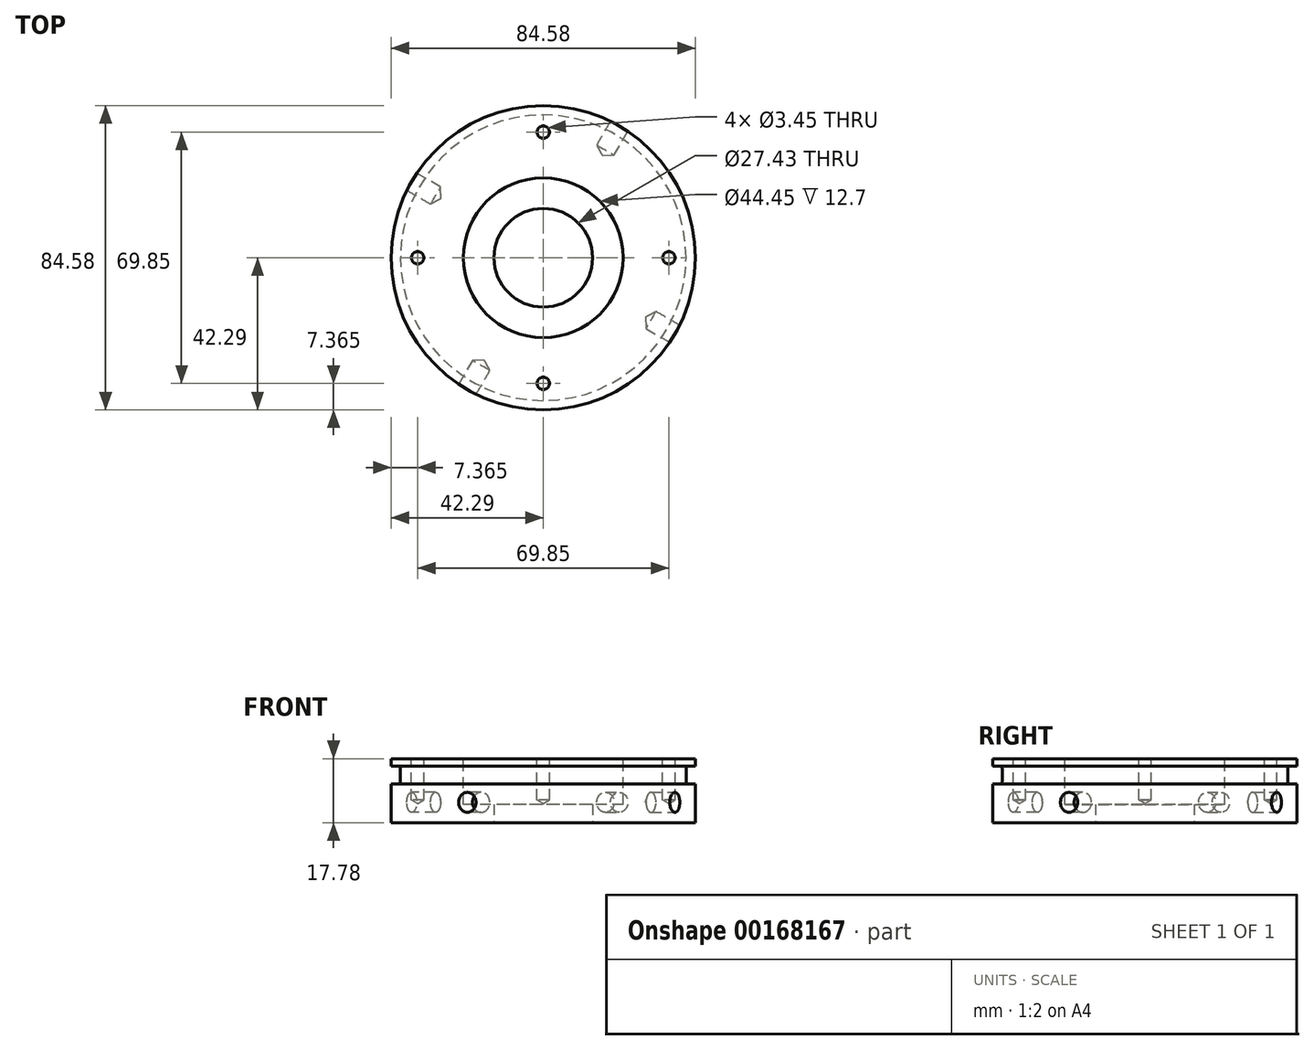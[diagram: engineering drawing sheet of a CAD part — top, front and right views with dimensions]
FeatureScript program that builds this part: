
annotation { "Feature Type Name" : "Feature", "Feature Type Description" : "" }
export const myFeature = defineFeature(function(context is Context, id is Id, definition is map)
    precondition{}
    {
        {
            var Q0;
            Q0=qCreatedBy(makeId("Top.planeOp"),FACE);
            var sketch = newSketch(context, id + "F0", { "sketchPlane" : qUnion([Q0])});
            skCircle(sketch, "E0", {"center": v(0, 0) * mm, "radius": 42.3 * mm});
            skSolve(sketch);
        }
        {
            var Q0;
            Q0=makeQuery(id+"F0.imprint","IMPRINT",FACE,{"disambiguationData":[TD([[makeQuery(id+"F0.imprint","IMPRINT",EDGE,{"derivedFrom":sQuery(id+"F0.wireOp",EDGE,"E0")}),1.0]])]});
            extrude(context, id + "F1", {"entities" : qUnion([Q0]), "depth" : 17.78 * mm});
        }
        {
            var Q0;
            {var subQ0=makeQuery(id+"FhJubWmbG7UBd7M_1.boolean.opBoolean","COPY",FACE,{"derivedFrom":makeQuery(id+"FhJubWmbG7UBd7M_1.opExtrude","SWEPT_FACE",FACE,{"disambiguationData":[OSD([sQuery(id+"FRuIeaWD6VeLny9_1.wireOp",EDGE,"idePJaX5-tPPE-BKw2-N1m4-zZUQrY6AHjir")])]})});Q0=makeQuery(id+"FOQC5dfjhO448EJ_1.boolean.opBoolean","SPLIT",FACE,{"disambiguationData":[TD([subQ0])],"derivedFrom":makeQuery(id+"FkcieFRIapZdHPD_1.boolean.opBoolean","SPLIT",FACE,{"disambiguationData":[TD([subQ0])],"derivedFrom":makeQuery(id+"F1.opExtrude","CAP_FACE",FACE,{"disambiguationData":[OSD([sQuery(id+"F0.wireOp",EDGE,"E0")])],"isStart":false})})});}
            var sketch = newSketch(context, id + "F2", { "sketchPlane" : qUnion([Q0])});
            skCircle(sketch, "E1", {"center": v(0, 0) * mm, "radius": 34.93 * mm, "construction": true});
            skLineSegment(sketch, "E2", {"start": v(0, 0) * mm, "end": v(34.93, 0) * mm, "construction": true});
            skPoint(sketch, "E3", {"position": v(34.93, 0) * mm});
            skPoint(sketch, "E4.1.0", {"position": v(0, 34.93) * mm});
            skPoint(sketch, "E4.2.0", {"position": v(-34.93, 0) * mm});
            skPoint(sketch, "E4.3.0", {"position": v(0, -34.93) * mm});
            skSolve(sketch);
        }
        {
            var Q0;
            Q0=sQuery(id+"F2.wireOp",VERTEX,"E3");
            var Q1;
            Q1=sQuery(id+"F2.wireOp",VERTEX,"E4.3.0");
            var Q2;
            Q2=sQuery(id+"F2.wireOp",VERTEX,"E4.2.0");
            var Q3;
            Q3=sQuery(id+"F2.wireOp",VERTEX,"E4.1.0");
            var Q4;
            Q4=makeQuery(id+"F1.opExtrude","SWEPT_BODY",BODY,{"disambiguationData":[OSD([sQuery(id+"F0.wireOp",EDGE,"E0")])]});
            hole(context, id + "F3", {"style" : HoleStyle.SIMPLE, "endStyle" : HoleEndStyle.BLIND, "standardTappedOrClearance" : lookupTablePath({ "standard" : "ANSI", "engagement" : "75%", "pitch" : "32 tpi", "size" : "#8", "type" : "Tapped" }), "standardBlindInLast" : lookupTablePath({ "standard" : "ANSI", "engagement" : "75%", "pitch" : "32 tpi", "size" : "#8", "type" : "Tapped" }), "holeDiameter" : 3.45 * mm, "holeDepth" : 11.43 * mm, "locations" : qUnion([Q0, Q1, Q2, Q3]), "scope" : qUnion([Q4]), "majorDiameter" : 4.17 * mm});
        }
        {
            var Q0;
            Q0=makeQuery(id+"FOQC5dfjhO448EJ_1.boolean.opBoolean","SPLIT",FACE,{"disambiguationData":[TD([makeQuery(id+"FhJubWmbG7UBd7M_1.boolean.opBoolean","COPY",FACE,{"derivedFrom":makeQuery(id+"FhJubWmbG7UBd7M_1.opExtrude","SWEPT_FACE",FACE,{"disambiguationData":[OSD([sQuery(id+"FRuIeaWD6VeLny9_1.wireOp",EDGE,"idePJaX5-tPPE-BKw2-N1m4-zZUQrY6AHjir")])]})})])],"derivedFrom":makeQuery(id+"F1.opExtrude","CAP_FACE",FACE,{"disambiguationData":[OSD([sQuery(id+"F0.wireOp",EDGE,"E0")])],"isStart":false})});
            cPlane(context, id + "F4", {"entities" : qUnion([Q0]), "cplaneType" : CPlaneType.OFFSET, "offset" : 2.03 * mm, "oppositeDirection" : true, "width" : 152.4 * mm, "height" : 152.4 * mm});
        }
        {
            var Q0;
            Q0=qCreatedBy(id+"F4.planeOp",FACE);
            var sketch = newSketch(context, id + "F5", { "sketchPlane" : qUnion([Q0])});
            skCircle(sketch, "E5", {"center": v(0, 0) * mm, "radius": 39.7 * mm});
            skCircle(sketch, "E6.0", {"center": v(0, 0) * mm, "radius": 42.3 * mm});
            skSolve(sketch);
        }
        {
            var Q0;
            Q0=qSketchRegion(id+"F5",true);
            extrude(context, id + "F6", {"entities" : qUnion([Q0]), "operationType" : NewBodyOperationType.REMOVE, "oppositeDirection" : true, "depth" : 5 * mm});
        }
        {
            var Q0;
            Q0=makeQuery(id+"F6.boolean.opBoolean","COPY",EDGE,{"derivedFrom":makeQuery(id+"F6.opExtrude","CAP_EDGE",EDGE,{"disambiguationData":[OSD([sQuery(id+"F5.wireOp",EDGE,"E5")])],"isStart":false})});
            var Q1;
            Q1=makeQuery(id+"F6.boolean.opBoolean","COPY",EDGE,{"derivedFrom":makeQuery(id+"F6.opExtrude","CAP_EDGE",EDGE,{"disambiguationData":[OSD([sQuery(id+"F5.wireOp",EDGE,"E5")])],"isStart":true})});
            fillet(context, id + "F7", {"entities" : qUnion([Q0, Q1]), "radius" : 0.76 * mm, "tangentPropagation" : true, "allowEdgeOverflow" : false});
        }
        {
            var Q0;
            {var subQ1=sQuery(id+"F0.wireOp",EDGE,"E0");var subQ2=makeQuery(id+"F1.opExtrude","SWEPT_FACE",FACE,{"disambiguationData":[OSD([subQ1])]});Q0=makeQuery(id+"FkcieFRIapZdHPD_1.boolean.opBoolean","SPLIT",FACE,{"disambiguationData":[TD([subQ2])],"derivedFrom":makeQuery(id+"F1.opExtrude","CAP_FACE",FACE,{"disambiguationData":[OSD([subQ1])],"isStart":false})});}
            var sketch = newSketch(context, id + "F8", { "sketchPlane" : qUnion([Q0])});
            skCircle(sketch, "E7.0", {"center": v(0, 0) * mm, "radius": 42.3 * mm, "construction": true});
            skPoint(sketch, "E8", {"position": v(-21.15, -36.63) * mm});
            skLineSegment(sketch, "E9", {"start": v(0, -42.3) * mm, "end": v(0, 0) * mm, "construction": true});
            skLineSegment(sketch, "E10", {"start": v(0, 0) * mm, "end": v(-17.96, -31.1) * mm, "construction": true});
            skLineSegment(sketch, "E11", {"start": v(-17.96, -31.1) * mm, "end": v(-21.15, -36.63) * mm, "construction": true});
            skLineSegment(sketch, "E12", {"start": v(0, 0) * mm, "end": v(21.15, 36.63) * mm, "construction": true});
            skLineSegment(sketch, "E13", {"start": v(21.15, 36.63) * mm, "end": v(0, 0) * mm, "construction": true});
            skLineSegment(sketch, "E14", {"start": v(36.63, -21.15) * mm, "end": v(0, 0) * mm, "construction": true});
            skLineSegment(sketch, "E15", {"start": v(0, 0) * mm, "end": v(-36.63, 21.15) * mm, "construction": true});
            skPoint(sketch, "E16", {"position": v(21.15, 36.63) * mm});
            skPoint(sketch, "E17", {"position": v(36.63, -21.15) * mm});
            skPoint(sketch, "E18", {"position": v(-36.63, 21.15) * mm});
            skSolve(sketch);
        }
        {
            var Q0;
            Q0=qCreatedBy(makeId("Front.planeOp"),FACE);
            var sketch = newSketch(context, id + "F9", { "sketchPlane" : qUnion([Q0])});
            skLineSegment(sketch, "E19", {"start": v(0, 0) * mm, "end": v(0, 38.57) * mm, "construction": true});
            skSolve(sketch);
        }
        {
            var Q0;
            Q0=sQuery(id+"F9.wireOp",EDGE,"E19");
            cPlane(context, id + "F10", {"entities" : qUnion([Q0]), "cplaneType" : CPlaneType.LINE_ANGLE, "offset" : 25.4 * mm, "angle" : 60 * degree, "width" : 152.4 * mm, "height" : 152.4 * mm});
        }
        {
            var Q0;
            Q0=sQuery(id+"F8.wireOp",VERTEX,"E8");
            var Q1;
            Q1=qCreatedBy(id+"F10.planeOp",FACE);
            cPlane(context, id + "F11", {"entities" : qUnion([Q0, Q1]), "cplaneType" : CPlaneType.PLANE_POINT, "offset" : 25.4 * mm, "width" : 152.4 * mm, "height" : 152.4 * mm});
        }
        {
            var Q0;
            Q0=qCreatedBy(id+"F11.planeOp",FACE);
            var Q1;
            Q1=sQuery(id+"F8.wireOp",VERTEX,"E16");
            cPlane(context, id + "F12", {"entities" : qUnion([Q0, Q1]), "cplaneType" : CPlaneType.PLANE_POINT, "offset" : 25.4 * mm, "width" : 152.4 * mm, "height" : 152.4 * mm});
        }
        {
            var Q0;
            Q0=sQuery(id+"F9.wireOp",EDGE,"E19");
            cPlane(context, id + "F13", {"entities" : qUnion([Q0]), "cplaneType" : CPlaneType.LINE_ANGLE, "offset" : 25.4 * mm, "angle" : 150 * degree, "width" : 152.4 * mm, "height" : 152.4 * mm});
        }
        {
            var Q0;
            Q0=sQuery(id+"F8.wireOp",VERTEX,"E18");
            var Q1;
            Q1=qCreatedBy(id+"F13.planeOp",FACE);
            cPlane(context, id + "F14", {"entities" : qUnion([Q0, Q1]), "cplaneType" : CPlaneType.PLANE_POINT, "offset" : 25.4 * mm, "width" : 152.4 * mm, "height" : 152.4 * mm});
        }
        {
            var Q0;
            Q0=qCreatedBy(id+"F13.planeOp",FACE);
            var Q1;
            Q1=sQuery(id+"F8.wireOp",VERTEX,"E17");
            cPlane(context, id + "F15", {"entities" : qUnion([Q0, Q1]), "cplaneType" : CPlaneType.PLANE_POINT, "offset" : 25.4 * mm, "width" : 152.4 * mm, "height" : 152.4 * mm});
        }
        {
            var Q0;
            Q0=qCreatedBy(id+"F11.planeOp",FACE);
            var sketch = newSketch(context, id + "F16", { "sketchPlane" : qUnion([Q0])});
            skLineSegment(sketch, "E20", {"start": v(0, 0) * mm, "end": v(0, 5.66) * mm, "construction": true});
            skPoint(sketch, "E21", {"position": v(0, 5.66) * mm});
            skSolve(sketch);
        }
        {
            var Q0;
            Q0=qCreatedBy(id+"F12.planeOp",FACE);
            var sketch = newSketch(context, id + "F17", { "sketchPlane" : qUnion([Q0])});
            skPoint(sketch, "E22", {"position": v(0, 5.66) * mm});
            skLineSegment(sketch, "E23.0", {"start": v(0, 0) * mm, "end": v(0, 5.66) * mm, "construction": true});
            skSolve(sketch);
        }
        {
            var Q0;
            Q0=qCreatedBy(id+"F14.planeOp",FACE);
            var sketch = newSketch(context, id + "F18", { "sketchPlane" : qUnion([Q0])});
            skLineSegment(sketch, "E24", {"start": v(0, 0) * mm, "end": v(0, 5.66) * mm, "construction": true});
            skLineSegment(sketch, "E25.0", {"start": v(-42.3, 0) * mm, "end": v(-42.3, 5.66) * mm, "construction": true});
            skPoint(sketch, "E26", {"position": v(0, 5.66) * mm});
            skLineSegment(sketch, "E27", {"start": v(-42.3, 5.66) * mm, "end": v(0, 5.66) * mm, "construction": true});
            skSolve(sketch);
        }
        {
            var Q0;
            Q0=qCreatedBy(id+"F15.planeOp",FACE);
            var sketch = newSketch(context, id + "F19", { "sketchPlane" : qUnion([Q0])});
            skLineSegment(sketch, "E28.0", {"start": v(0, 0) * mm, "end": v(0, 5.66) * mm, "construction": true});
            skPoint(sketch, "E29", {"position": v(0, 5.66) * mm});
            skSolve(sketch);
        }
        {
            var Q0;
            Q0=sQuery(id+"F19.wireOp",VERTEX,"E29");
            var Q1;
            Q1=makeQuery(id+"F1.opExtrude","SWEPT_BODY",BODY,{"disambiguationData":[OSD([sQuery(id+"F0.wireOp",EDGE,"E0")])]});
            hole(context, id + "F20", {"style" : HoleStyle.SIMPLE, "endStyle" : HoleEndStyle.BLIND, "oppositeDirection" : true, "standardTappedOrClearance" : lookupTablePath({ "standard" : "ANSI", "engagement" : "75%", "pitch" : "32 tpi", "size" : "1/4", "type" : "Tapped" }), "standardBlindInLast" : lookupTablePath({ "standard" : "ANSI", "engagement" : "75%", "pitch" : "32 tpi", "size" : "1/4", "type" : "Tapped" }), "holeDiameter" : 5.56 * mm, "holeDepth" : 7.62 * mm, "locations" : qUnion([Q0]), "scope" : qUnion([Q1]), "majorDiameter" : 6.35 * mm});
        }
        {
            var Q0;
            Q0=sQuery(id+"F18.wireOp",VERTEX,"E26");
            var Q1;
            Q1=makeQuery(id+"F1.opExtrude","SWEPT_BODY",BODY,{"disambiguationData":[OSD([sQuery(id+"F0.wireOp",EDGE,"E0")])]});
            hole(context, id + "F21", {"style" : HoleStyle.SIMPLE, "endStyle" : HoleEndStyle.BLIND, "standardTappedOrClearance" : lookupTablePath({ "standard" : "ANSI", "engagement" : "75%", "pitch" : "32 tpi", "size" : "1/4", "type" : "Tapped" }), "standardBlindInLast" : lookupTablePath({ "standard" : "ANSI", "engagement" : "75%", "pitch" : "32 tpi", "size" : "1/4", "type" : "Tapped" }), "holeDiameter" : 5.56 * mm, "holeDepth" : 7.62 * mm, "locations" : qUnion([Q0]), "scope" : qUnion([Q1]), "majorDiameter" : 6.35 * mm});
        }
        {
            var Q0;
            Q0=sQuery(id+"F16.wireOp",VERTEX,"E21");
            var Q1;
            Q1=makeQuery(id+"F1.opExtrude","SWEPT_BODY",BODY,{"disambiguationData":[OSD([sQuery(id+"F0.wireOp",EDGE,"E0")])]});
            hole(context, id + "F22", {"style" : HoleStyle.SIMPLE, "endStyle" : HoleEndStyle.BLIND, "oppositeDirection" : true, "standardTappedOrClearance" : lookupTablePath({ "standard" : "ANSI", "engagement" : "75%", "pitch" : "32 tpi", "size" : "1/4", "type" : "Tapped" }), "standardBlindInLast" : lookupTablePath({ "standard" : "ANSI", "engagement" : "75%", "pitch" : "32 tpi", "size" : "1/4", "type" : "Tapped" }), "holeDiameter" : 5.56 * mm, "holeDepth" : 7.62 * mm, "locations" : qUnion([Q0]), "scope" : qUnion([Q1]), "majorDiameter" : 6.35 * mm});
        }
        {
            var Q0;
            Q0=sQuery(id+"F17.wireOp",VERTEX,"E22");
            var Q1;
            Q1=makeQuery(id+"F1.opExtrude","SWEPT_BODY",BODY,{"disambiguationData":[OSD([sQuery(id+"F0.wireOp",EDGE,"E0")])]});
            hole(context, id + "F23", {"style" : HoleStyle.SIMPLE, "endStyle" : HoleEndStyle.BLIND, "standardTappedOrClearance" : lookupTablePath({ "standard" : "ANSI", "engagement" : "75%", "pitch" : "32 tpi", "size" : "1/4", "type" : "Tapped" }), "standardBlindInLast" : lookupTablePath({ "standard" : "ANSI", "engagement" : "75%", "pitch" : "32 tpi", "size" : "1/4", "type" : "Tapped" }), "holeDiameter" : 5.56 * mm, "holeDepth" : 7.62 * mm, "locations" : qUnion([Q0]), "scope" : qUnion([Q1]), "majorDiameter" : 6.35 * mm});
        }
        {
            var Q0;
            Q0=makeQuery(id+"F1.opExtrude","CAP_FACE",FACE,{"disambiguationData":[OSD([sQuery(id+"F0.wireOp",EDGE,"E0")])],"isStart":true});
            var sketch = newSketch(context, id + "F24", { "sketchPlane" : qUnion([Q0])});
            skPoint(sketch, "E30", {"position": v(0, 0) * mm});
            skSolve(sketch);
        }
        {
            var Q0;
            Q0=sQuery(id+"F24.wireOp",VERTEX,"E30");
            var Q1;
            Q1=makeQuery(id+"F1.opExtrude","SWEPT_BODY",BODY,{"disambiguationData":[OSD([sQuery(id+"F0.wireOp",EDGE,"E0")])]});
            hole(context, id + "F25", {"style" : HoleStyle.SIMPLE, "endStyle" : HoleEndStyle.THROUGH, "holeDiameter" : 27.43 * mm, "locations" : qUnion([Q0]), "scope" : qUnion([Q1]), "isTappedThrough" : true});
        }
        {
            var Q0;
            Q0=makeQuery(id+"F1.opExtrude","CAP_FACE",FACE,{"disambiguationData":[OSD([sQuery(id+"F0.wireOp",EDGE,"E0")])],"isStart":false});
            var sketch = newSketch(context, id + "F26", { "sketchPlane" : qUnion([Q0])});
            skCircle(sketch, "E31", {"center": v(0, 0) * mm, "radius": 22.23 * mm});
            skSolve(sketch);
        }
        {
            var Q0;
            Q0=qSketchRegion(id+"F26",true);
            var Q1;
            Q1=sQuery(id+"F26.wireOp",EDGE,"E31");
            extrude(context, id + "F27", {"entities" : qUnion([Q0]), "operationType" : NewBodyOperationType.REMOVE, "surfaceEntities" : qUnion([Q1]), "oppositeDirection" : true, "depth" : 12.7 * mm});
        }
    });
